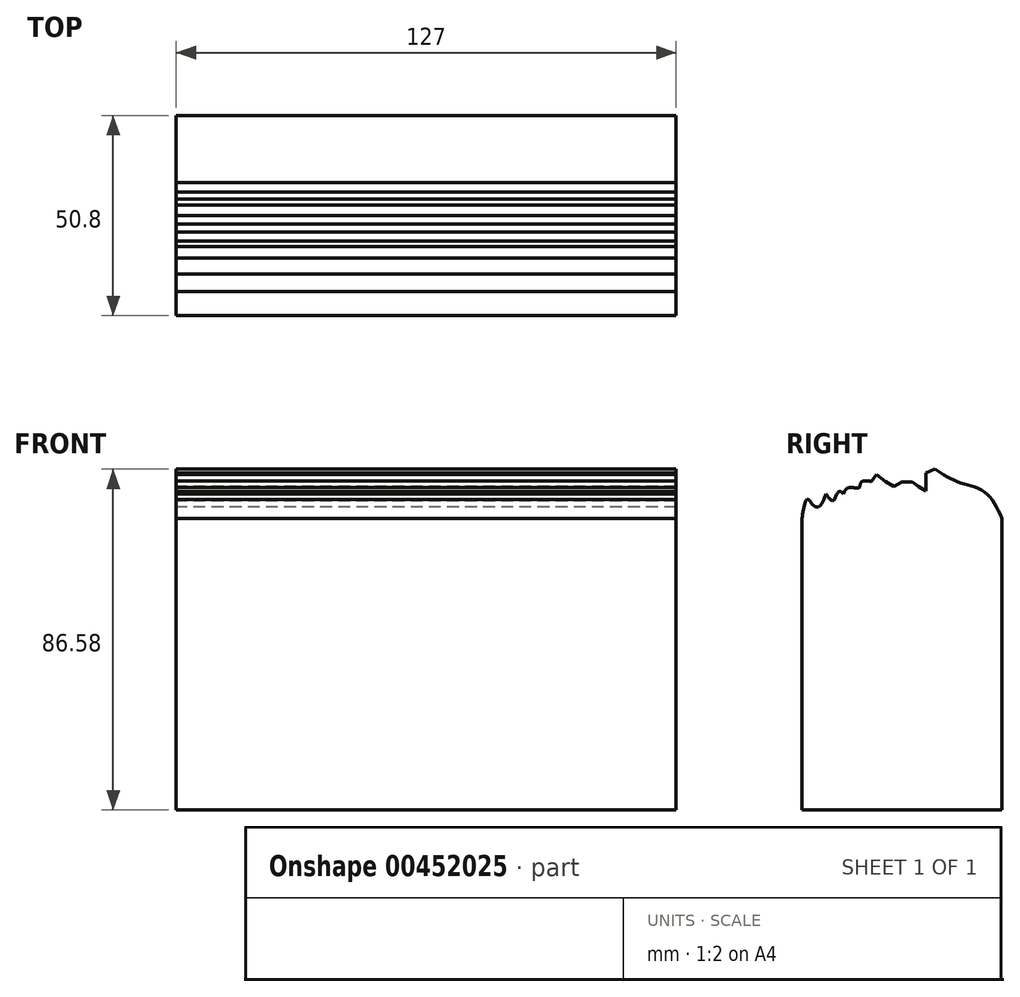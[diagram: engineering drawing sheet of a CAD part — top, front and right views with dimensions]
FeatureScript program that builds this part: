
annotation { "Feature Type Name" : "Feature", "Feature Type Description" : "" }
export const myFeature = defineFeature(function(context is Context, id is Id, definition is map)
    precondition{}
    {
        {
            var Q0;
            Q0=qCreatedBy(makeId("Right.planeOp"),FACE);
            var sketch = newSketch(context, id + "F0", { "sketchPlane" : qUnion([Q0])});
            skLineSegment(sketch, "E0.bottom", {"start": v(-25.4, -37.02) * mm, "end": v(25.4, -37.02) * mm});
            skLineSegment(sketch, "E0.top", {"start": v(-25.4, 37.02) * mm, "end": v(25.4, 37.02) * mm});
            skLineSegment(sketch, "E0.left", {"start": v(-25.4, -37.02) * mm, "end": v(-25.4, 37.02) * mm});
            skLineSegment(sketch, "E0.right", {"start": v(25.4, -37.02) * mm, "end": v(25.4, 37.02) * mm});
            skPoint(sketch, "E0.middle", {"position": v(0, 0) * mm});
            skFitSpline(sketch, "E1", {"points": [v(25.4, 37.02) * mm, v(20.9, 43.81) * mm, v(14.37, 46.26) * mm, v(8.34, 49.56) * mm], "startDerivative": vector(-10.69, 22.78) * mm, "endDerivative": vector(-17.84, 11.69) * mm});
            skLineSegment(sketch, "E2", {"start": v(8.34, 49.56) * mm, "end": v(6.01, 48.6) * mm});
            skLineSegment(sketch, "E3", {"start": v(6.01, 48.6) * mm, "end": v(6.01, 44.01) * mm});
            skLineSegment(sketch, "E4", {"start": v(6.01, 44.01) * mm, "end": v(4.18, 45.08) * mm});
            skLineSegment(sketch, "E5", {"start": v(4.18, 45.08) * mm, "end": v(2.63, 46.33) * mm});
            skLineSegment(sketch, "E6", {"start": v(2.63, 46.33) * mm, "end": v(0, 46.33) * mm});
            skLineSegment(sketch, "E7", {"start": v(0, 46.33) * mm, "end": v(-2.11, 45.11) * mm});
            skLineSegment(sketch, "E8", {"start": v(-2.11, 45.11) * mm, "end": v(-4.16, 46.47) * mm});
            skLineSegment(sketch, "E9", {"start": v(-4.16, 46.47) * mm, "end": v(-6.5, 48.2) * mm});
            skLineSegment(sketch, "E10", {"start": v(-6.5, 48.2) * mm, "end": v(-7.83, 46.4) * mm});
            skFitSpline(sketch, "E11", {"points": [v(-7.83, 46.4) * mm, v(-10.17, 46.4) * mm, v(-10.8, 44.84) * mm], "startDerivative": vector(-5.13, 0.92) * mm, "endDerivative": vector(-0.7, -4.2) * mm});
            skFitSpline(sketch, "E12", {"points": [v(-10.8, 44.84) * mm, v(-14.9, 43.19) * mm], "startDerivative": vector(-4.1, -1.65) * mm, "endDerivative": vector(-3.2, -8.78) * mm});
            skFitSpline(sketch, "E13", {"points": [v(-14.9, 43.19) * mm, v(-17.35, 41.64) * mm, v(-19.3, 43.19) * mm], "startDerivative": vector(-8.55, 11.98) * mm, "endDerivative": vector(-3.83, 4.56) * mm});
            skFitSpline(sketch, "E14", {"points": [v(-19.3, 43.19) * mm, v(-23.77, 41.79) * mm, v(-25.4, 37.02) * mm], "startDerivative": vector(-12.88, -37.7) * mm, "endDerivative": vector(-1.7, -11.02) * mm});
            skSolve(sketch);
        }
        {
            var Q0;
            Q0 = qSketchRegion(id + "F0", true);
            extrude(context, id + "F1", {"entities" : qUnion([Q0]), "depth" : 127 * mm, "offsetDistance" : 25.4 * mm});
        }
    });
